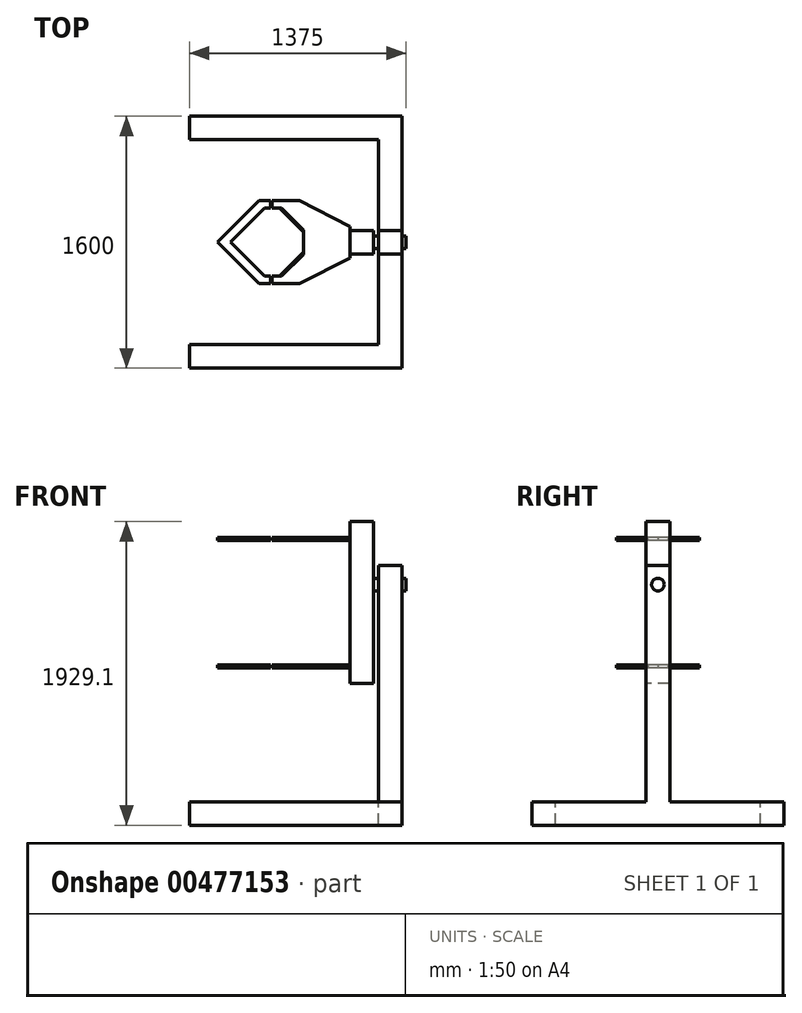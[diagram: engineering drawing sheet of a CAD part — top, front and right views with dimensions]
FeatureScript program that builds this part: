
annotation { "Feature Type Name" : "Feature", "Feature Type Description" : "" }
export const myFeature = defineFeature(function(context is Context, id is Id, definition is map)
    precondition{}
    {
        {
            var Q0;
            Q0=qCreatedBy(makeId("Top.planeOp"),FACE);
            var sketch = newSketch(context, id + "F0", { "sketchPlane" : qUnion([Q0])});
            skCircle(sketch, "E0", {"center": v(0, 0) * mm, "radius": 186.1 * mm});
            skLineSegment(sketch, "E1", {"start": v(0, 263.19) * mm, "end": v(263.19, 0) * mm});
            skLineSegment(sketch, "E2", {"start": v(263.19, 0) * mm, "end": v(0, -263.19) * mm});
            skLineSegment(sketch, "E3", {"start": v(0, -263.19) * mm, "end": v(496.1, -263.19) * mm});
            skLineSegment(sketch, "E4", {"start": v(0, 263.19) * mm, "end": v(496.1, 263.19) * mm});
            skLineSegment(sketch, "E5", {"start": v(496.1, 263.19) * mm, "end": v(496.1, -263.19) * mm});
            skLineSegment(sketch, "E6", {"start": v(199.99, 63.2) * mm, "end": v(199.99, -63.2) * mm});
            skLineSegment(sketch, "E7", {"start": v(47.19, 216) * mm, "end": v(0, 216) * mm});
            skLineSegment(sketch, "E8", {"start": v(0, 216) * mm, "end": v(0, 263.19) * mm});
            skLineSegment(sketch, "E9", {"start": v(0, -263.19) * mm, "end": v(0, -216) * mm});
            skLineSegment(sketch, "E10", {"start": v(0, -216) * mm, "end": v(47.19, -216) * mm});
            skLineSegment(sketch, "E11", {"start": v(175.03, 263.19) * mm, "end": v(496.1, 100) * mm});
            skLineSegment(sketch, "E12", {"start": v(175.03, -263.19) * mm, "end": v(496.1, -100) * mm});
            skLineSegment(sketch, "E13", {"start": v(0, 263.19) * mm, "end": v(-263.19, 0) * mm});
            skLineSegment(sketch, "E14", {"start": v(-263.19, 0) * mm, "end": v(0, -263.19) * mm});
            skLineSegment(sketch, "E15", {"start": v(0, 263.19) * mm, "end": v(-84.1, 263.19) * mm});
            skLineSegment(sketch, "E16", {"start": v(-84.1, 263.19) * mm, "end": v(-347.3, 0) * mm});
            skLineSegment(sketch, "E17", {"start": v(-347.3, 0) * mm, "end": v(-84.1, -263.19) * mm});
            skLineSegment(sketch, "E18", {"start": v(-84.1, -263.19) * mm, "end": v(0, -263.19) * mm});
            skLineSegment(sketch, "E19", {"start": v(0, 216) * mm, "end": v(-47.19, 216) * mm});
            skLineSegment(sketch, "E20", {"start": v(0, -216) * mm, "end": v(-47.19, -216) * mm});
            skLineSegment(sketch, "E21", {"start": v(-8.66, 263.19) * mm, "end": v(-8.66, 216) * mm});
            skLineSegment(sketch, "E22", {"start": v(-8.66, -216) * mm, "end": v(-8.66, -263.19) * mm});
            skSolve(sketch);
        }
        {
            var Q0;
            {var subQ3=sQuery(id+"F0.wireOp",EDGE,"E11");Q0=makeQuery(id+"F0.imprint","IMPRINT",FACE,{"disambiguationData":[TD([[makeQuery(id+"F0.imprint","IMPRINT",EDGE,{"derivedFrom":subQ3}),-1.0]])]});}
            var Q1;
            {var subQ2=sQuery(id+"F0.wireOp",EDGE,"E7");Q1=makeQuery(id+"F0.imprint","IMPRINT",FACE,{"disambiguationData":[TD([[makeQuery(id+"F0.imprint","IMPRINT",EDGE,{"derivedFrom":subQ2}),-1.0]])]});}
            var Q2;
            {var subQ3=sQuery(id+"F0.wireOp",EDGE,"E6");Q2=makeQuery(id+"F0.imprint","IMPRINT",FACE,{"disambiguationData":[TD([[makeQuery(id+"F0.imprint","IMPRINT",EDGE,{"derivedFrom":subQ3}),1.0]])]});}
            var Q3;
            {var subQ0=sQuery(id+"F0.wireOp",EDGE,"E9");Q3=makeQuery(id+"F0.imprint","IMPRINT",FACE,{"disambiguationData":[TD([[makeQuery(id+"F0.imprint","IMPRINT",EDGE,{"derivedFrom":subQ0}),-1.0]])]});}
            var Q4;
            {var subQ1=sQuery(id+"F0.wireOp",EDGE,"E16");Q4=makeQuery(id+"F0.imprint","IMPRINT",FACE,{"disambiguationData":[TD([[makeQuery(id+"F0.imprint","IMPRINT",EDGE,{"derivedFrom":subQ1}),1.0]])]});}
            var Q5;
            {var subQ0=sQuery(id+"F0.wireOp",EDGE,"E19");var subQ1=sQuery(id+"F0.wireOp",EDGE,"E13");var subQ2=makeQuery(id+"F0.imprint","INTERSECT",VERTEX,{"derivedFrom":[subQ1,subQ0]});Q5=makeQuery(id+"F0.imprint","IMPRINT",FACE,{"disambiguationData":[TD([[makeQuery(id+"F0.imprint","IMPRINT",EDGE,{"disambiguationData":[TD([[subQ2,1.0]])],"derivedFrom":subQ1}),1.0]])]});}
            var Q6;
            {var subQ0=sQuery(id+"F0.wireOp",EDGE,"E20");var subQ1=sQuery(id+"F0.wireOp",EDGE,"E14");var subQ2=makeQuery(id+"F0.imprint","INTERSECT",VERTEX,{"derivedFrom":[subQ1,subQ0]});Q6=makeQuery(id+"F0.imprint","IMPRINT",FACE,{"disambiguationData":[TD([[makeQuery(id+"F0.imprint","IMPRINT",EDGE,{"disambiguationData":[TD([[subQ2,-1.0]])],"derivedFrom":subQ1}),1.0]])]});}
            extrude(context, id + "F1", {"entities" : qUnion([Q0, Q1, Q2, Q3, Q4, Q5, Q6]), "depth" : 20 * mm, "offsetDistance" : 25 * mm});
        }
        {
            var Q0;
            Q0=makeQuery(id+"F1.opExtrude","SWEPT_BODY",BODY,{"disambiguationData":[OSD([sQuery(id+"F0.wireOp",EDGE,"E1"),sQuery(id+"F0.wireOp",EDGE,"E2"),sQuery(id+"F0.wireOp",EDGE,"E3"),sQuery(id+"F0.wireOp",EDGE,"E4"),sQuery(id+"F0.wireOp",EDGE,"E5"),sQuery(id+"F0.wireOp",EDGE,"E6"),sQuery(id+"F0.wireOp",EDGE,"E7"),sQuery(id+"F0.wireOp",EDGE,"E8"),sQuery(id+"F0.wireOp",EDGE,"E9"),sQuery(id+"F0.wireOp",EDGE,"E10"),sQuery(id+"F0.wireOp",EDGE,"E11"),sQuery(id+"F0.wireOp",EDGE,"E12")])]});
            var Q1;
            Q1=makeQuery(id+"F1.opExtrude","SWEPT_BODY",BODY,{"disambiguationData":[OSD([sQuery(id+"F0.wireOp",EDGE,"E13"),sQuery(id+"F0.wireOp",EDGE,"E14"),sQuery(id+"F0.wireOp",EDGE,"E15"),sQuery(id+"F0.wireOp",EDGE,"E16"),sQuery(id+"F0.wireOp",EDGE,"E17"),sQuery(id+"F0.wireOp",EDGE,"E18"),sQuery(id+"F0.wireOp",EDGE,"E19"),sQuery(id+"F0.wireOp",EDGE,"E20"),sQuery(id+"F0.wireOp",EDGE,"E21"),sQuery(id+"F0.wireOp",EDGE,"E22")])]});
            transform(context, id + "F2", {"entities" : qUnion([Q0, Q1]), "transformType" : TransformType.TRANSLATION_3D, "dx" : 0 * mm, "dy" : 0 * mm, "dz" : 809.1 * mm, "makeCopy" : true});
        }
        {
            var Q0;
            Q0=makeQuery(id+"F2.opPattern","COPY",FACE,{"derivedFrom":makeQuery(id+"F1.opExtrude","CAP_FACE",FACE,{"disambiguationData":[OSD([sQuery(id+"F0.wireOp",EDGE,"E1"),sQuery(id+"F0.wireOp",EDGE,"E2"),sQuery(id+"F0.wireOp",EDGE,"E3"),sQuery(id+"F0.wireOp",EDGE,"E4"),sQuery(id+"F0.wireOp",EDGE,"E5"),sQuery(id+"F0.wireOp",EDGE,"E6"),sQuery(id+"F0.wireOp",EDGE,"E7"),sQuery(id+"F0.wireOp",EDGE,"E8"),sQuery(id+"F0.wireOp",EDGE,"E9"),sQuery(id+"F0.wireOp",EDGE,"E10"),sQuery(id+"F0.wireOp",EDGE,"E11"),sQuery(id+"F0.wireOp",EDGE,"E12")])],"isStart":false}),"instanceName":"1"});
            var sketch = newSketch(context, id + "F3", { "sketchPlane" : qUnion([Q0])});
            skLineSegment(sketch, "E23.bottom", {"start": v(496.1, 75) * mm, "end": v(646.1, 75) * mm});
            skLineSegment(sketch, "E23.top", {"start": v(496.1, -75) * mm, "end": v(646.1, -75) * mm});
            skLineSegment(sketch, "E23.left", {"start": v(496.1, 75) * mm, "end": v(496.1, -75) * mm});
            skLineSegment(sketch, "E23.right", {"start": v(646.1, 75) * mm, "end": v(646.1, -75) * mm});
            skSolve(sketch);
        }
        {
            var Q0;
            Q0 = qSketchRegion(id + "F3", true);
            extrude(context, id + "F4", {"entities" : qUnion([Q0]), "depth" : 100 * mm, "hasSecondDirection" : true, "secondDirectionOppositeDirection" : true, "secondDirectionDepth" : 929.1 * mm});
        }
        {
            var Q0;
            Q0=makeQuery(id+"F4.opExtrude","SWEPT_FACE",FACE,{"disambiguationData":[OSD([sQuery(id+"F3.wireOp",EDGE,"E23.right")])]});
            var sketch = newSketch(context, id + "F5", { "sketchPlane" : qUnion([Q0])});
            skCircle(sketch, "E24", {"center": v(0, 529.1) * mm, "radius": 40 * mm});
            skSolve(sketch);
        }
        {
            var Q0;
            Q0 = qSketchRegion(id + "F5", true);
            extrude(context, id + "F6", {"entities" : qUnion([Q0]), "operationType" : NewBodyOperationType.ADD, "depth" : 30 * mm});
        }
        {
            var Q0;
            Q0=qCreatedBy(makeId("Top.planeOp"),FACE);
            cPlane(context, id + "F7", {"entities" : qUnion([Q0]), "cplaneType" : CPlaneType.OFFSET, "offset" : 650 * mm, "width" : 150 * mm, "height" : 150 * mm});
        }
        {
            var Q0;
            Q0=qCreatedBy(id+"F7.planeOp",FACE);
            var sketch = newSketch(context, id + "F8", { "sketchPlane" : qUnion([Q0])});
            skLineSegment(sketch, "E25.bottom", {"start": v(676.1, 75) * mm, "end": v(826.1, 75) * mm});
            skLineSegment(sketch, "E25.top", {"start": v(676.1, -75) * mm, "end": v(826.1, -75) * mm});
            skLineSegment(sketch, "E25.left", {"start": v(676.1, 75) * mm, "end": v(676.1, -75) * mm});
            skLineSegment(sketch, "E25.right", {"start": v(826.1, 75) * mm, "end": v(826.1, -75) * mm});
            skSolve(sketch);
        }
        {
            var Q0;
            Q0=makeQuery(id+"F8.imprint","IMPRINT",FACE,{"disambiguationData":[TD([[makeQuery(id+"F8.imprint","IMPRINT",EDGE,{"derivedFrom":sQuery(id+"F8.wireOp",EDGE,"E25.bottom")}),-1.0]])]});
            extrude(context, id + "F9", {"entities" : qUnion([Q0]), "oppositeDirection" : true, "depth" : 1500 * mm});
        }
        {
            var Q0;
            Q0=makeQuery(id+"F9.opExtrude","CAP_FACE",FACE,{"disambiguationData":[OSD([sQuery(id+"F8.wireOp",EDGE,"E25.bottom"),sQuery(id+"F8.wireOp",EDGE,"E25.top"),sQuery(id+"F8.wireOp",EDGE,"E25.left"),sQuery(id+"F8.wireOp",EDGE,"E25.right")])],"isStart":false});
            var sketch = newSketch(context, id + "F10", { "sketchPlane" : qUnion([Q0])});
            skLineSegment(sketch, "E26.bottom", {"start": v(676.1, 800) * mm, "end": v(826.1, 800) * mm});
            skLineSegment(sketch, "E26.top", {"start": v(676.1, -800) * mm, "end": v(826.1, -800) * mm});
            skLineSegment(sketch, "E26.left", {"start": v(676.1, 800) * mm, "end": v(676.1, -800) * mm});
            skLineSegment(sketch, "E26.right", {"start": v(826.1, 800) * mm, "end": v(826.1, -800) * mm});
            skLineSegment(sketch, "E27.bottom", {"start": v(676.1, 800) * mm, "end": v(-523.9, 800) * mm});
            skLineSegment(sketch, "E27.top", {"start": v(676.1, 650) * mm, "end": v(-523.9, 650) * mm});
            skLineSegment(sketch, "E27.left", {"start": v(676.1, 800) * mm, "end": v(676.1, 650) * mm});
            skLineSegment(sketch, "E27.right", {"start": v(-523.9, 800) * mm, "end": v(-523.9, 650) * mm});
            skLineSegment(sketch, "E28.bottom", {"start": v(676.1, -800) * mm, "end": v(-523.9, -800) * mm});
            skLineSegment(sketch, "E28.top", {"start": v(676.1, -650) * mm, "end": v(-523.9, -650) * mm});
            skLineSegment(sketch, "E28.left", {"start": v(676.1, -800) * mm, "end": v(676.1, -650) * mm});
            skLineSegment(sketch, "E28.right", {"start": v(-523.9, -800) * mm, "end": v(-523.9, -650) * mm});
            skSolve(sketch);
        }
        {
            var Q0;
            Q0 = qSketchRegion(id + "F10", true);
            extrude(context, id + "F11", {"entities" : qUnion([Q0]), "operationType" : NewBodyOperationType.ADD, "depth" : 150 * mm});
        }
        {
            var Q0;
            Q0=makeQuery(id+"F2.opPattern","COPY",EDGE,{"derivedFrom":makeQuery(id+"F1.opExtrude","CAP_EDGE",EDGE,{"disambiguationData":[OSD([sQuery(id+"F0.wireOp",EDGE,"E2")])],"isStart":false}),"instanceName":"1"});
            var Q1;
            Q1=makeQuery(id+"F2.opPattern","COPY",EDGE,{"derivedFrom":makeQuery(id+"F1.opExtrude","CAP_EDGE",EDGE,{"disambiguationData":[OSD([sQuery(id+"F0.wireOp",EDGE,"E1")])],"isStart":false}),"instanceName":"1"});
            chamfer(context, id + "F12", {"entities" : qUnion([Q0, Q1]), "width" : 10 * mm, "tangentPropagation" : true});
        }
        {
            var Q0;
            Q0=makeQuery(id+"F11.boolean.opBoolean","MERGE",FACE,{"derivedFrom":[makeQuery(id+"F9.opExtrude","SWEPT_FACE",FACE,{"disambiguationData":[OSD([sQuery(id+"F8.wireOp",EDGE,"E25.right")])]}),makeQuery(id+"F11.opExtrude","SWEPT_FACE",FACE,{"disambiguationData":[OSD([sQuery(id+"F10.wireOp",EDGE,"E26.right")])]})]});
            var sketch = newSketch(context, id + "F13", { "sketchPlane" : qUnion([Q0])});
            skCircle(sketch, "E29", {"center": v(0, 529.1) * mm, "radius": 40 * mm});
            skSolve(sketch);
        }
        {
            var Q0;
            Q0 = qSketchRegion(id + "F13", true);
            extrude(context, id + "F14", {"entities" : qUnion([Q0]), "depth" : 25 * mm});
        }
    });
